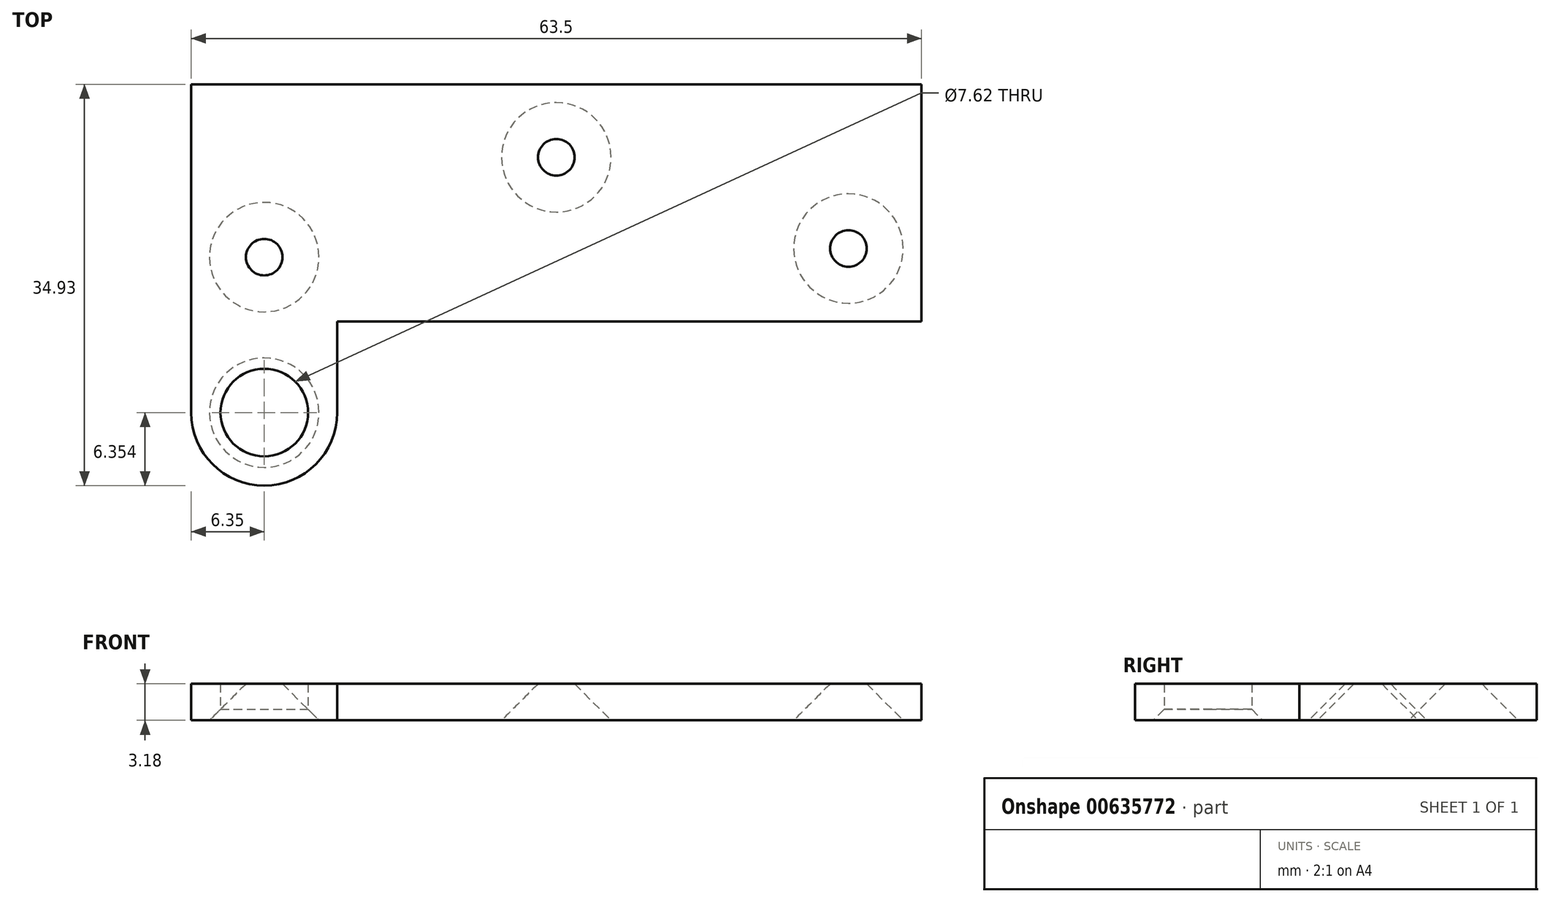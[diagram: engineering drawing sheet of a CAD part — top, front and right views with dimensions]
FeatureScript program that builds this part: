
annotation { "Feature Type Name" : "Feature", "Feature Type Description" : "" }
export const myFeature = defineFeature(function(context is Context, id is Id, definition is map)
    precondition{}
    {
        {
            var Q0;
            Q0=qCreatedBy(makeId("Top.planeOp"),FACE);
            var sketch = newSketch(context, id + "F0", { "sketchPlane" : qUnion([Q0])});
            skLineSegment(sketch, "E0.bottom", {"start": v(31.75, 10.32) * mm, "end": v(-31.75, 10.32) * mm});
            skLineSegment(sketch, "E0.top", {"start": v(31.75, -10.32) * mm, "end": v(-19.05, -10.32) * mm});
            skLineSegment(sketch, "E0.left", {"start": v(31.75, 10.32) * mm, "end": v(31.75, -10.32) * mm});
            skPoint(sketch, "E0.middle", {"position": v(0, 0) * mm});
            skArc(sketch, "E1", {"start": v(-31.75, -18.26) * mm, "mid": v(-25.4, -24.6) * mm, "end": v(-19.05, -18.26) * mm});
            skLineSegment(sketch, "E2", {"start": v(-19.05, -18.26) * mm, "end": v(-19.05, -10.32) * mm});
            skLineSegment(sketch, "E3", {"start": v(-31.75, 10.32) * mm, "end": v(-31.75, -18.26) * mm});
            skPoint(sketch, "E4", {"position": v(25.4, -3.97) * mm});
            skPoint(sketch, "E5", {"position": v(0, 3.97) * mm});
            skPoint(sketch, "E6", {"position": v(-25.4, -4.72) * mm});
            skSolve(sketch);
        }
        {
            var Q0;
            Q0=makeQuery(id+"F0.imprint","IMPRINT",FACE,{"disambiguationData":[TD([[makeQuery(id+"F0.imprint","IMPRINT",EDGE,{"derivedFrom":sQuery(id+"F0.wireOp",EDGE,"E0.bottom")}),1.0]])]});
            extrude(context, id + "F1", {"entities" : qUnion([Q0]), "depth" : 3.17 * mm, "offsetDistance" : 25.4 * mm});
        }
        {
            var Q0;
            Q0=sQuery(id+"F0.wireOp",VERTEX,"E4");
            var Q1;
            Q1=sQuery(id+"F0.wireOp",VERTEX,"E5");
            var Q2;
            Q2=sQuery(id+"F0.wireOp",VERTEX,"E6");
            var Q3;
            Q3=makeQuery(id+"F1.opExtrude","SWEPT_BODY",BODY,{"disambiguationData":[OSD([sQuery(id+"F0.wireOp",EDGE,"E0.bottom"),sQuery(id+"F0.wireOp",EDGE,"E0.top"),sQuery(id+"F0.wireOp",EDGE,"E0.left"),sQuery(id+"F0.wireOp",EDGE,"E1"),sQuery(id+"F0.wireOp",EDGE,"E2"),sQuery(id+"F0.wireOp",EDGE,"E3")])]});
            hole(context, id + "F2", {"style" : HoleStyle.C_SINK, "endStyle" : HoleEndStyle.THROUGH, "oppositeDirection" : true, "holeDiameter" : 2.54 * mm, "cSinkDiameter" : 9.52 * mm, "cSinkAngle" : 90 * degree, "majorDiameter" : 6.35 * mm, "isTappedThrough" : true, "tappedDepth" : 12.7 * mm, "tapClearance" : 3, "locations" : qUnion([Q0, Q1, Q2]), "scope" : qUnion([Q3])});
        }
        {
            var Q0;
            Q0=sQuery(id+"F0.wireOp",VERTEX,"E1.center");
            var Q1;
            Q1=makeQuery(id+"F1.opExtrude","SWEPT_BODY",BODY,{"disambiguationData":[OSD([sQuery(id+"F0.wireOp",EDGE,"E0.bottom"),sQuery(id+"F0.wireOp",EDGE,"E0.top"),sQuery(id+"F0.wireOp",EDGE,"E0.left"),sQuery(id+"F0.wireOp",EDGE,"E1"),sQuery(id+"F0.wireOp",EDGE,"E2"),sQuery(id+"F0.wireOp",EDGE,"E3")])]});
            hole(context, id + "F3", {"style" : HoleStyle.C_SINK, "endStyle" : HoleEndStyle.THROUGH, "oppositeDirection" : true, "holeDiameter" : 7.62 * mm, "cSinkDiameter" : 9.52 * mm, "cSinkAngle" : 90 * degree, "majorDiameter" : 6.35 * mm, "isTappedThrough" : true, "tappedDepth" : 12.7 * mm, "tapClearance" : 3, "locations" : qUnion([Q0]), "scope" : qUnion([Q1])});
        }
    });
